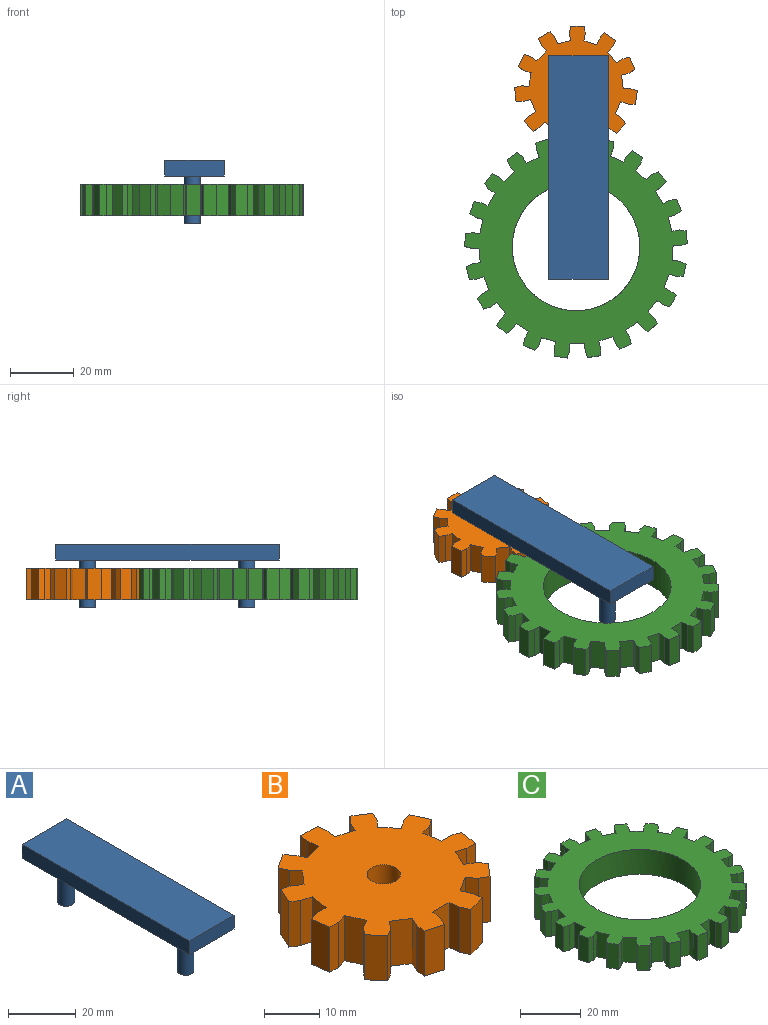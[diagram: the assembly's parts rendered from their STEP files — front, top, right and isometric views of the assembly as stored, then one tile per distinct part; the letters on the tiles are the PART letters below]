
ASSEMBLY  parts=3 mates=2
PART A: 10 faces, bbox 18.7x70.1x20 mm
  f0: plane 18.73x5mm, normal (0,1,0), area 93.7mm2, adj f1,f3,f4,f5
  f1: plane 70.05x5mm, normal (-1,0,0), area 350.3mm2, adj f0,f2,f4,f5
  f2: plane 18.73x5mm, normal (0,-1,0), area 93.7mm2, adj f1,f3,f4,f5
  f3: plane 70.05x5mm, normal (1,0,0), area 350.3mm2, adj f0,f2,f4,f5
  f4: plane 70.05x18.73mm, normal (0,0,1), area 1312.1mm2, adj f0,f1,f2,f3
  f5: plane 70.05x18.73mm, normal (0,0,-1), area 1272.8mm2, adj f0,f1,f2,f3,f6,f8
  f6: cylinder r=2.5mm len=15mm, axis (0,0,1), area 235.6mm2, adj f5,f7
  f7: plane 5x5mm, normal (0,0,-1), area 19.6mm2, adj f6
  f8: cylinder r=2.5mm len=15mm, axis (0,0,1), area 235.6mm2, adj f5,f9
  f9: plane 5x5mm, normal (0,0,-1), area 19.6mm2, adj f8
PART B: 69 faces, bbox 38.5x38.1x10 mm
  f0: plane 10x2.39mm, normal (-0.99,-0.14,0), area 24.1mm2, adj f1,f6,f7,f14
  f1: plane 10x1.96mm, normal (-0.9,-0.43,0), area 21.7mm2, adj f0,f2,f6,f7
  f2: plane 10x4.06mm, normal (0.28,-0.96,0), area 42.3mm2, adj f1,f3,f6,f7
  f3: plane 10x2.15mm, normal (0.99,0.13,0), area 21.7mm2, adj f2,f4,f6,f7
  f4: plane 10x2.19mm, normal (0.91,0.42,0), area 24.1mm2, adj f3,f5,f6,f7
  f5: plane 10x3.54mm, normal (0.54,-0.84,0), area 42.1mm2, adj f4,f6,f7,f8
  f6: plane 38.52x38.13mm, normal (0,0,1), area 875.3mm2, adj f0,f1,f2,f3,f4,f5,f8,f9
  f7: plane 38.52x38.13mm, normal (0,0,-1), area 875.3mm2, adj f0,f1,f2,f3,f4,f5,f8,f9
  f8: plane 10x1.82mm, normal (-0.76,-0.65,0), area 24.1mm2, adj f5,f6,f7,f63
  f9: plane 10x2.19mm, normal (-0.91,0.42,0), area 24.1mm2, adj f6,f7,f10,f20
  f10: plane 10x2.15mm, normal (-0.99,0.13,0), area 21.7mm2, adj f6,f7,f9,f11
  f11: plane 10x4.06mm, normal (-0.28,-0.96,0), area 42.3mm2, adj f6,f7,f10,f12
  f12: plane 10x1.96mm, normal (0.9,-0.43,0), area 21.7mm2, adj f6,f7,f11,f13
  f13: plane 10x2.39mm, normal (0.99,-0.14,0), area 24.1mm2, adj f6,f7,f12,f14
  f14: plane 10x4.21mm, normal (0,-1,0), area 42.1mm2, adj f0,f6,f7,f13
  f15: plane 10x2.03mm, normal (-0.54,0.84,0), area 24.1mm2, adj f6,f7,f16,f26
  f16: plane 10x1.65mm, normal (-0.76,0.65,0), area 21.7mm2, adj f6,f7,f15,f17
  f17: plane 10x3.2mm, normal (-0.76,-0.65,0), area 42.3mm2, adj f6,f7,f16,f18
  f18: plane 10x1.84mm, normal (0.53,-0.85,0), area 21.7mm2, adj f6,f7,f17,f19
  f19: plane 10x1.82mm, normal (0.76,-0.65,0), area 24.1mm2, adj f6,f7,f18,f20
  f20: plane 10x3.54mm, normal (-0.54,-0.84,0), area 42.1mm2, adj f6,f7,f9,f19
  f21: plane 10x2.41mm, normal (0,1,0), area 24.1mm2, adj f6,f7,f22,f32
  f22: plane 10x2.07mm, normal (-0.29,0.96,0), area 21.7mm2, adj f6,f7,f21,f23
  f23: plane 10x4.18mm, normal (-0.99,-0.14,0), area 42.3mm2, adj f6,f7,f22,f24
  f24: plane 10x2.17mm, normal (-0.01,-1,0), area 21.7mm2, adj f6,f7,f23,f25
  f25: plane 10x2.31mm, normal (0.28,-0.96,0), area 24.1mm2, adj f6,f7,f24,f26
  f26: plane 10x3.83mm, normal (-0.91,-0.42,0), area 42.1mm2, adj f6,f7,f15,f25
  f27: plane 10x2.03mm, normal (0.54,0.84,0), area 24.1mm2, adj f6,f7,f28,f38
  f28: plane 10x2.09mm, normal (0.27,0.96,0), area 21.7mm2, adj f6,f7,f27,f29
  f29: plane 10x3.85mm, normal (-0.91,0.42,0), area 42.3mm2, adj f6,f7,f28,f30
  f30: plane 10x1.81mm, normal (-0.55,-0.84,0), area 21.7mm2, adj f6,f7,f29,f31
  f31: plane 10x2.31mm, normal (-0.28,-0.96,0), area 24.1mm2, adj f6,f7,f30,f32
  f32: plane 10x4.16mm, normal (-0.99,0.14,0), area 42.1mm2, adj f6,f7,f21,f31
  f33: plane 10x2.19mm, normal (0.91,0.42,0), area 24.1mm2, adj f6,f7,f34,f44
  f34: plane 10x1.62mm, normal (0.75,0.66,0), area 21.7mm2, adj f6,f7,f33,f35
  f35: plane 10x3.56mm, normal (-0.54,0.84,0), area 42.3mm2, adj f6,f7,f34,f36
  f36: plane 10x1.98mm, normal (-0.91,-0.41,0), area 21.7mm2, adj f6,f7,f35,f37
  f37: plane 10x1.82mm, normal (-0.76,-0.65,0), area 24.1mm2, adj f6,f7,f36,f38
  f38: plane 10x3.18mm, normal (-0.76,0.65,0), area 42.1mm2, adj f6,f7,f27,f37
  f39: plane 10x2.39mm, normal (0.99,-0.14,0), area 24.1mm2, adj f6,f7,f40,f50
  f40: plane 10x2.14mm, normal (0.99,0.15,0), area 21.7mm2, adj f6,f7,f39,f41
  f41: plane 10x4.23mm, normal (0,1,0), area 42.3mm2, adj f6,f7,f40,f42
  f42: plane 10x2.14mm, normal (-0.99,0.15,0), area 21.7mm2, adj f6,f7,f41,f43
  f43: plane 10x2.39mm, normal (-0.99,-0.14,0), area 24.1mm2, adj f6,f7,f42,f44
  f44: plane 10x4.04mm, normal (-0.28,0.96,0), area 42.1mm2, adj f6,f7,f33,f43
  f45: plane 10x1.82mm, normal (0.76,-0.65,0), area 24.1mm2, adj f6,f7,f46,f56
  f46: plane 10x1.98mm, normal (0.91,-0.41,0), area 21.7mm2, adj f6,f7,f45,f47
  f47: plane 10x3.56mm, normal (0.54,0.84,0), area 42.3mm2, adj f6,f7,f46,f48
  f48: plane 10x1.62mm, normal (-0.75,0.66,0), area 21.7mm2, adj f6,f7,f47,f49
  f49: plane 10x2.19mm, normal (-0.91,0.42,0), area 24.1mm2, adj f6,f7,f48,f50
  f50: plane 10x4.04mm, normal (0.28,0.96,0), area 42.1mm2, adj f6,f7,f39,f49
  f51: plane 10x2.31mm, normal (0.28,-0.96,0), area 24.1mm2, adj f6,f7,f52,f62
  f52: plane 10x1.81mm, normal (0.55,-0.84,0), area 21.7mm2, adj f6,f7,f51,f53
  f53: plane 10x3.85mm, normal (0.91,0.42,0), area 42.3mm2, adj f6,f7,f52,f54
  f54: plane 10x2.09mm, normal (-0.27,0.96,0), area 21.7mm2, adj f6,f7,f53,f55
  f55: plane 10x2.03mm, normal (-0.54,0.84,0), area 24.1mm2, adj f6,f7,f54,f56
  f56: plane 10x3.18mm, normal (0.76,0.65,0), area 42.1mm2, adj f6,f7,f45,f55
  f57: plane 10x2.31mm, normal (-0.28,-0.96,0), area 24.1mm2, adj f6,f7,f58,f67
  f58: plane 10x2.17mm, normal (0.01,-1,0), area 21.7mm2, adj f6,f7,f57,f59
  f59: plane 10x4.18mm, normal (0.99,-0.14,0), area 42.3mm2, adj f6,f7,f58,f60
  f60: plane 10x2.07mm, normal (0.29,0.96,0), area 21.7mm2, adj f6,f7,f59,f61
  f61: plane 10x2.41mm, normal (0,1,0), area 24.1mm2, adj f6,f7,f60,f62
  f62: plane 10x4.16mm, normal (0.99,0.14,0), area 42.1mm2, adj f6,f7,f51,f61
  f63: plane 10x1.84mm, normal (-0.53,-0.85,0), area 21.7mm2, adj f6,f7,f8,f64
  f64: plane 10x3.2mm, normal (0.76,-0.65,0), area 42.3mm2, adj f6,f7,f63,f65
  f65: plane 10x1.65mm, normal (0.76,0.65,0), area 21.7mm2, adj f6,f7,f64,f66
  f66: plane 10x2.03mm, normal (0.54,0.84,0), area 24.1mm2, adj f6,f7,f65,f67
  f67: plane 10x3.83mm, normal (0.91,-0.42,0), area 42.1mm2, adj f6,f7,f57,f66
  f68: cylinder r=3mm len=10mm, axis (0,0,-1), area 188.5mm2, adj f6,f7
PART C: 129 faces, bbox 69.8x69.6x10 mm
  f0: plane 10x2.4mm, normal (-1,-0.07,0), area 24.1mm2, adj f1,f5,f6,f7
  f1: plane 10x4.49mm, normal (-0.15,0.99,0), area 45.4mm2, adj f0,f6,f7,f8
  f2: plane 10x2.4mm, normal (1,-0.07,0), area 24.1mm2, adj f3,f6,f7,f10
  f3: plane 10x2.12mm, normal (0.98,0.22,0), area 21.7mm2, adj f2,f4,f6,f7
  f4: plane 10x3.95mm, normal (0,1,0), area 39.5mm2, adj f3,f5,f6,f7
  f5: plane 10x2.12mm, normal (-0.98,0.22,0), area 21.7mm2, adj f0,f4,f6,f7
  f6: plane 69.78x69.59mm, normal (0,0,1), area 2071.7mm2, adj f0,f1,f2,f3,f4,f5,f8,f9
  f7: plane 69.78x69.59mm, normal (0,0,-1), area 2071.7mm2, adj f0,f1,f2,f3,f4,f5,f8,f9
  f8: plane 10x2.35mm, normal (0.97,0.22,0), area 24.1mm2, adj f1,f6,f7,f125
  f9: plane 10x2.35mm, normal (-0.97,0.22,0), area 24.1mm2, adj f6,f7,f10,f14
  f10: plane 10x4.49mm, normal (0.15,0.99,0), area 45.4mm2, adj f2,f6,f7,f9
  f11: plane 10x2.24mm, normal (0.93,-0.37,0), area 24.1mm2, adj f6,f7,f12,f16
  f12: plane 10x2.17mm, normal (1,-0.08,0), area 21.7mm2, adj f6,f7,f11,f13
  f13: plane 10x3.77mm, normal (0.29,0.96,0), area 39.5mm2, adj f6,f7,f12,f14
  f14: plane 10x1.88mm, normal (-0.87,0.5,0), area 21.7mm2, adj f6,f7,f9,f13
  f15: plane 10x2.09mm, normal (-0.87,0.5,0), area 24.1mm2, adj f6,f7,f16,f20
  f16: plane 10x4.09mm, normal (0.43,0.9,0), area 45.4mm2, adj f6,f7,f11,f15
  f17: plane 10x1.88mm, normal (0.78,-0.62,0), area 24.1mm2, adj f6,f7,f18,f22
  f18: plane 10x2.02mm, normal (0.93,-0.37,0), area 21.7mm2, adj f6,f7,f17,f19
  f19: plane 10x3.26mm, normal (0.56,0.83,0), area 39.5mm2, adj f6,f7,f18,f20
  f20: plane 10x1.59mm, normal (-0.68,0.73,0), area 21.7mm2, adj f6,f7,f15,f19
  f21: plane 10x1.77mm, normal (-0.68,0.73,0), area 24.1mm2, adj f6,f7,f22,f26
  f22: plane 10x3.33mm, normal (0.68,0.73,0), area 45.4mm2, adj f6,f7,f17,f21
  f23: plane 10x1.99mm, normal (0.56,-0.83,0), area 24.1mm2, adj f6,f7,f24,f28
  f24: plane 10x1.7mm, normal (0.78,-0.63,0), area 21.7mm2, adj f6,f7,f23,f25
  f25: plane 10x3.09mm, normal (0.78,0.62,0), area 39.5mm2, adj f6,f7,f24,f26
  f26: plane 10x1.96mm, normal (-0.44,0.9,0), area 21.7mm2, adj f6,f7,f21,f25
  f27: plane 10x2.17mm, normal (-0.43,0.9,0), area 24.1mm2, adj f6,f7,f28,f32
  f28: plane 10x3.94mm, normal (0.87,0.5,0), area 45.4mm2, adj f6,f7,f23,f27
  f29: plane 10x2.3mm, normal (0.29,-0.96,0), area 24.1mm2, adj f6,f7,f30,f34
  f30: plane 10x1.8mm, normal (0.56,-0.83,0), area 21.7mm2, adj f6,f7,f29,f31
  f31: plane 10x3.68mm, normal (0.93,0.37,0), area 39.5mm2, adj f6,f7,f30,f32
  f32: plane 10x2.15mm, normal (-0.15,0.99,0), area 21.7mm2, adj f6,f7,f27,f31
  f33: plane 10x2.38mm, normal (-0.15,0.99,0), area 24.1mm2, adj f6,f7,f34,f38
  f34: plane 10x4.43mm, normal (0.97,0.22,0), area 45.4mm2, adj f6,f7,f29,f33
  f35: plane 10x2.41mm, normal (0,-1,0), area 24.1mm2, adj f6,f7,f36,f40
  f36: plane 10x2.08mm, normal (0.29,-0.96,0), area 21.7mm2, adj f6,f7,f35,f37
  f37: plane 10x3.94mm, normal (1,0.07,0), area 39.5mm2, adj f6,f7,f36,f38
  f38: plane 10x2.15mm, normal (0.15,0.99,0), area 21.7mm2, adj f6,f7,f33,f37
  f39: plane 10x2.38mm, normal (0.15,0.99,0), area 24.1mm2, adj f6,f7,f40,f44
  f40: plane 10x4.53mm, normal (1,-0.07,0), area 45.4mm2, adj f6,f7,f35,f39
  f41: plane 10x2.3mm, normal (-0.29,-0.96,0), area 24.1mm2, adj f6,f7,f42,f46
  f42: plane 10x2.17mm, normal (0,-1,0), area 21.7mm2, adj f6,f7,f41,f43
  f43: plane 10x3.85mm, normal (0.97,-0.22,0), area 39.5mm2, adj f6,f7,f42,f44
  f44: plane 10x1.96mm, normal (0.43,0.9,0), area 21.7mm2, adj f6,f7,f39,f43
  f45: plane 10x2.17mm, normal (0.43,0.9,0), area 24.1mm2, adj f6,f7,f46,f50
  f46: plane 10x4.23mm, normal (0.93,-0.37,0), area 45.4mm2, adj f6,f7,f41,f45
  f47: plane 10x1.99mm, normal (-0.56,-0.83,0), area 24.1mm2, adj f6,f7,f48,f52
  f48: plane 10x2.07mm, normal (-0.3,-0.95,0), area 21.7mm2, adj f6,f7,f47,f49
  f49: plane 10x3.42mm, normal (0.87,-0.5,0), area 39.5mm2, adj f6,f7,f48,f50
  f50: plane 10x1.6mm, normal (0.68,0.73,0), area 21.7mm2, adj f6,f7,f45,f49
  f51: plane 10x1.77mm, normal (0.68,0.73,0), area 24.1mm2, adj f6,f7,f52,f56
  f52: plane 10x3.55mm, normal (0.78,-0.62,0), area 45.4mm2, adj f6,f7,f47,f51
  f53: plane 10x1.88mm, normal (-0.78,-0.62,0), area 24.1mm2, adj f6,f7,f54,f58
  f54: plane 10x1.79mm, normal (-0.57,-0.82,0), area 21.7mm2, adj f6,f7,f53,f55
  f55: plane 10x2.89mm, normal (0.68,-0.73,0), area 39.5mm2, adj f6,f7,f54,f56
  f56: plane 10x1.88mm, normal (0.86,0.5,0), area 21.7mm2, adj f6,f7,f51,f55
  f57: plane 10x2.09mm, normal (0.87,0.5,0), area 24.1mm2, adj f6,f7,f58,f62
  f58: plane 10x3.75mm, normal (0.56,-0.83,0), area 45.4mm2, adj f6,f7,f53,f57
  f59: plane 10x2.24mm, normal (-0.93,-0.37,0), area 24.1mm2, adj f6,f7,f60,f64
  f60: plane 10x1.7mm, normal (-0.78,-0.62,0), area 21.7mm2, adj f6,f7,f59,f61
  f61: plane 10x3.56mm, normal (0.43,-0.9,0), area 39.5mm2, adj f6,f7,f60,f62
  f62: plane 10x2.12mm, normal (0.97,0.22,0), area 21.7mm2, adj f6,f7,f57,f61
  f63: plane 10x2.35mm, normal (0.97,0.22,0), area 24.1mm2, adj f6,f7,f64,f68
  f64: plane 10x4.34mm, normal (0.29,-0.96,0), area 45.4mm2, adj f6,f7,f59,f63
  f65: plane 10x2.4mm, normal (-1,-0.07,0), area 24.1mm2, adj f6,f7,f66,f70
  f66: plane 10x2.02mm, normal (-0.93,-0.36,0), area 21.7mm2, adj f6,f7,f65,f67
  f67: plane 10x3.9mm, normal (0.15,-0.99,0), area 39.5mm2, adj f6,f7,f66,f68
  f68: plane 10x2.17mm, normal (1,-0.07,0), area 21.7mm2, adj f6,f7,f63,f67
  f69: plane 10x2.4mm, normal (1,-0.07,0), area 24.1mm2, adj f6,f7,f70,f74
  f70: plane 10x4.54mm, normal (0,-1,0), area 45.4mm2, adj f6,f7,f65,f69
  f71: plane 10x2.35mm, normal (-0.97,0.22,0), area 24.1mm2, adj f6,f7,f72,f76
  f72: plane 10x2.17mm, normal (-1,-0.07,0), area 21.7mm2, adj f6,f7,f71,f73
  f73: plane 10x3.9mm, normal (-0.15,-0.99,0), area 39.5mm2, adj f6,f7,f72,f74
  f74: plane 10x2.02mm, normal (0.93,-0.36,0), area 21.7mm2, adj f6,f7,f69,f73
  f75: plane 10x2.24mm, normal (0.93,-0.37,0), area 24.1mm2, adj f6,f7,f76,f80
  f76: plane 10x4.34mm, normal (-0.29,-0.96,0), area 45.4mm2, adj f6,f7,f71,f75
  f77: plane 10x2.09mm, normal (-0.87,0.5,0), area 24.1mm2, adj f6,f7,f78,f82
  f78: plane 10x2.12mm, normal (-0.97,0.22,0), area 21.7mm2, adj f6,f7,f77,f79
  f79: plane 10x3.56mm, normal (-0.43,-0.9,0), area 39.5mm2, adj f6,f7,f78,f80
  f80: plane 10x1.7mm, normal (0.78,-0.62,0), area 21.7mm2, adj f6,f7,f75,f79
  f81: plane 10x1.88mm, normal (0.78,-0.62,0), area 24.1mm2, adj f6,f7,f82,f86
  f82: plane 10x3.75mm, normal (-0.56,-0.83,0), area 45.4mm2, adj f6,f7,f77,f81
  f83: plane 10x1.77mm, normal (-0.68,0.73,0), area 24.1mm2, adj f6,f7,f84,f88
  f84: plane 10x1.88mm, normal (-0.86,0.5,0), area 21.7mm2, adj f6,f7,f83,f85
  f85: plane 10x2.89mm, normal (-0.68,-0.73,0), area 39.5mm2, adj f6,f7,f84,f86
  f86: plane 10x1.79mm, normal (0.57,-0.82,0), area 21.7mm2, adj f6,f7,f81,f85
  f87: plane 10x1.99mm, normal (0.56,-0.83,0), area 24.1mm2, adj f6,f7,f88,f92
  f88: plane 10x3.55mm, normal (-0.78,-0.62,0), area 45.4mm2, adj f6,f7,f83,f87
  f89: plane 10x2.17mm, normal (-0.43,0.9,0), area 24.1mm2, adj f6,f7,f90,f94
  f90: plane 10x1.6mm, normal (-0.68,0.73,0), area 21.7mm2, adj f6,f7,f89,f91
  f91: plane 10x3.42mm, normal (-0.87,-0.5,0), area 39.5mm2, adj f6,f7,f90,f92
  f92: plane 10x2.07mm, normal (0.3,-0.95,0), area 21.7mm2, adj f6,f7,f87,f91
  f93: plane 10x2.3mm, normal (0.29,-0.96,0), area 24.1mm2, adj f6,f7,f94,f98
  f94: plane 10x4.23mm, normal (-0.93,-0.37,0), area 45.4mm2, adj f6,f7,f89,f93
  f95: plane 10x2.38mm, normal (-0.15,0.99,0), area 24.1mm2, adj f6,f7,f96,f100
  f96: plane 10x1.96mm, normal (-0.43,0.9,0), area 21.7mm2, adj f6,f7,f95,f97
  f97: plane 10x3.85mm, normal (-0.97,-0.22,0), area 39.5mm2, adj f6,f7,f96,f98
  f98: plane 10x2.17mm, normal (0,-1,0), area 21.7mm2, adj f6,f7,f93,f97
  f99: plane 10x2.41mm, normal (0,-1,0), area 24.1mm2, adj f6,f7,f100,f104
  f100: plane 10x4.53mm, normal (-1,-0.07,0), area 45.4mm2, adj f6,f7,f95,f99
  f101: plane 10x2.38mm, normal (0.15,0.99,0), area 24.1mm2, adj f6,f7,f102,f106
  f102: plane 10x2.15mm, normal (-0.15,0.99,0), area 21.7mm2, adj f6,f7,f101,f103
  f103: plane 10x3.94mm, normal (-1,0.07,0), area 39.5mm2, adj f6,f7,f102,f104
  f104: plane 10x2.08mm, normal (-0.29,-0.96,0), area 21.7mm2, adj f6,f7,f99,f103
  f105: plane 10x2.3mm, normal (-0.29,-0.96,0), area 24.1mm2, adj f6,f7,f106,f110
  f106: plane 10x4.43mm, normal (-0.97,0.22,0), area 45.4mm2, adj f6,f7,f101,f105
  f107: plane 10x2.17mm, normal (0.43,0.9,0), area 24.1mm2, adj f6,f7,f108,f112
  f108: plane 10x2.15mm, normal (0.15,0.99,0), area 21.7mm2, adj f6,f7,f107,f109
  f109: plane 10x3.68mm, normal (-0.93,0.37,0), area 39.5mm2, adj f6,f7,f108,f110
  f110: plane 10x1.8mm, normal (-0.56,-0.83,0), area 21.7mm2, adj f6,f7,f105,f109
  f111: plane 10x1.99mm, normal (-0.56,-0.83,0), area 24.1mm2, adj f6,f7,f112,f116
  f112: plane 10x3.94mm, normal (-0.87,0.5,0), area 45.4mm2, adj f6,f7,f107,f111
  f113: plane 10x1.77mm, normal (0.68,0.73,0), area 24.1mm2, adj f6,f7,f114,f118
  f114: plane 10x1.96mm, normal (0.44,0.9,0), area 21.7mm2, adj f6,f7,f113,f115
  f115: plane 10x3.09mm, normal (-0.78,0.62,0), area 39.5mm2, adj f6,f7,f114,f116
  f116: plane 10x1.7mm, normal (-0.78,-0.63,0), area 21.7mm2, adj f6,f7,f111,f115
  f117: plane 10x1.88mm, normal (-0.78,-0.62,0), area 24.1mm2, adj f6,f7,f118,f122
  f118: plane 10x3.33mm, normal (-0.68,0.73,0), area 45.4mm2, adj f6,f7,f113,f117
  f119: plane 10x2.09mm, normal (0.87,0.5,0), area 24.1mm2, adj f6,f7,f120,f124
  f120: plane 10x1.59mm, normal (0.68,0.73,0), area 21.7mm2, adj f6,f7,f119,f121
  f121: plane 10x3.26mm, normal (-0.56,0.83,0), area 39.5mm2, adj f6,f7,f120,f122
  f122: plane 10x2.02mm, normal (-0.93,-0.37,0), area 21.7mm2, adj f6,f7,f117,f121
  f123: plane 10x2.24mm, normal (-0.93,-0.37,0), area 24.1mm2, adj f6,f7,f124,f127
  f124: plane 10x4.09mm, normal (-0.43,0.9,0), area 45.4mm2, adj f6,f7,f119,f123
  f125: plane 10x1.88mm, normal (0.87,0.5,0), area 21.7mm2, adj f6,f7,f8,f126
  f126: plane 10x3.77mm, normal (-0.29,0.96,0), area 39.5mm2, adj f6,f7,f125,f127
  f127: plane 10x2.17mm, normal (-1,-0.08,0), area 21.7mm2, adj f6,f7,f123,f126
  f128: cylinder r=20mm len=40mm, axis (0,0,-1), area 1256.6mm2, adj f6,f7
PLACE A t=(-14.72,-19.57,10.32)mm fixed
PLACE B rot(axis=(0,0,1),162.2deg) t=(0.55,78.04,-2.18)mm
PLACE C rot(axis=(0,0,-1),136.4deg) t=(-14.72,-19.57,-2.18)mm
MATE revolute B.f68 <-> A.f6  axis (0,0,-1) through (-14.72,30.43,2.82)mm
MATE revolute C.f128 <-> A.f8  axis (0,0,-1) through (-14.72,-19.57,2.82)mm
